# Revit family: Thorn CETUS3 MSF
name_source: partatom
category: Lighting Fixtures
revit_build: Autodesk Revit 2018 (Build: 20170223_1515(x64)
units: mm (PartAtom-declared; Revit-internal decimal feet)

## family parameters
Cut with Voids When Loaded = No
Host = Face
Light Source = Yes
OmniClass Number = 23.80.70.11
OmniClass Title = Luminaries for Internal Lighting
Part Type = Normal
Room Calculation Point = No
Round Connector Dimension = Use Diameter
Shared = No

## types (1)
- CETUS3 MSF 2000
    Apparent Load = 16 VA
    Assembly Code = D5020210
    Body = ZG_Metal_White
    Color Filter = 16777215
    Default Elevation = 0 mm  [stored 0 ft]
    Description = Surface mount LED luminaire
    Dimming Lamp Color Temperature Shift = <None>
    Emit Shape Visible in Rendering = No
    Emit from Circle Diameter = 149 mm  [stored 0.488845 ft]
    Height = 182 mm  [stored 0.597113 ft]
    Lamp = LED
    Length = 181 mm  [stored 0.593832 ft]
    Manufacturer = Thorn Lighting
    Model = 92943894
    Photometric Web File = 92943894.IES
    Tilt Angle = -90.00°
    URL = www.thornlighting.com/92943894
    Voltage = 230 V
    Width = 181 mm  [stored 0.593832 ft]

note: [stored X ft] marks values corroborated as IEEE doubles in the binary element streams (Revit-internal decimal feet)

## geometry (parser evidence)
native form markers: Sweep x3
no freeform markers — native parametric forms only
